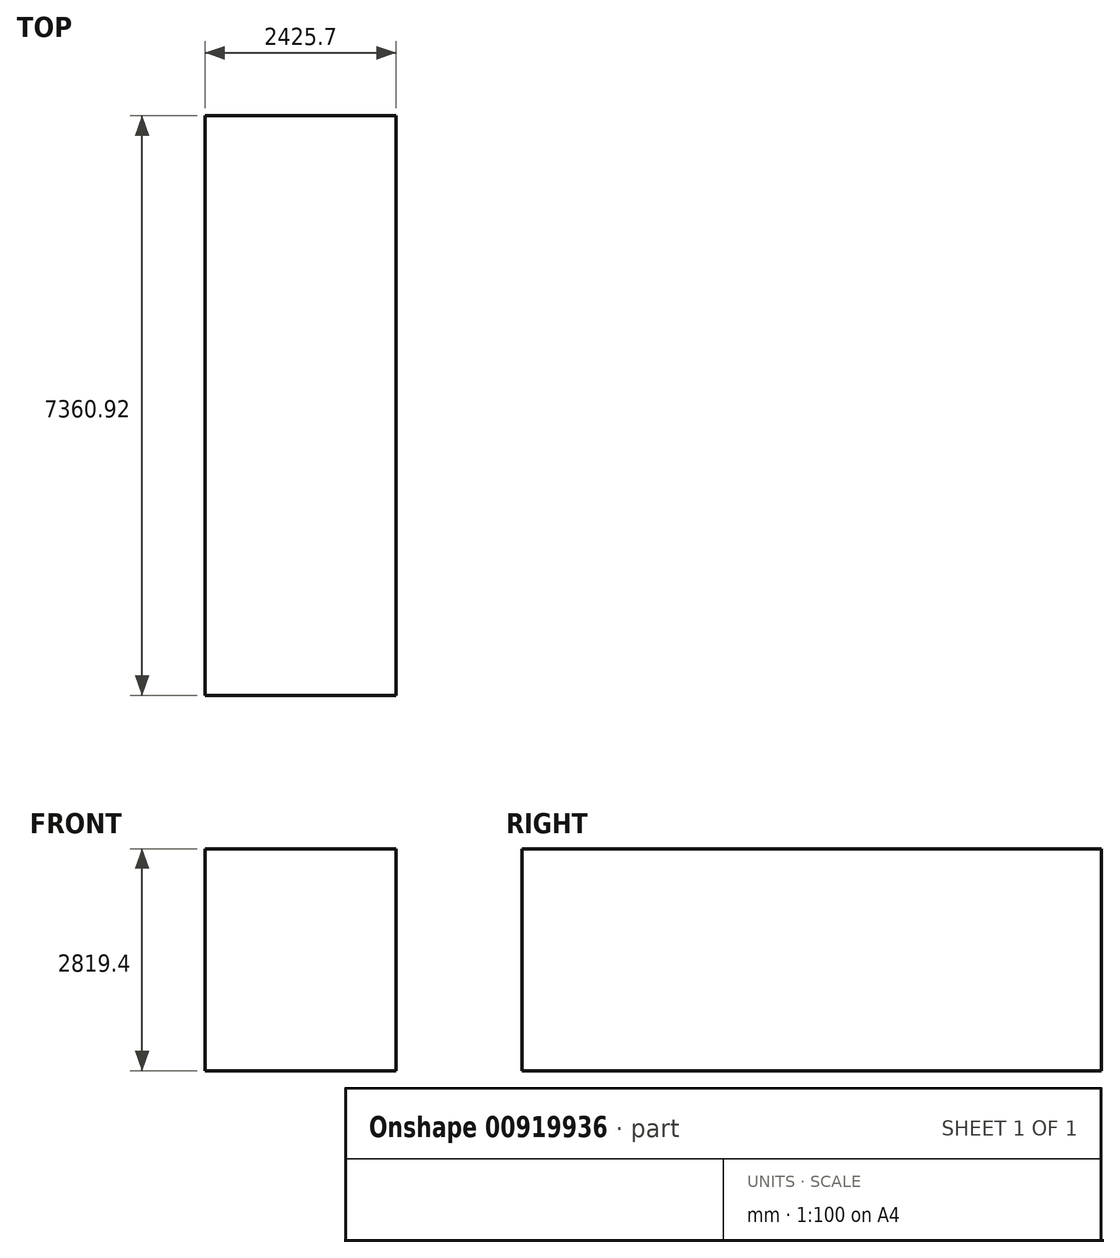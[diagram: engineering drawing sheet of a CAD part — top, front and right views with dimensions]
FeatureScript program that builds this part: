
annotation { "Feature Type Name" : "Feature", "Feature Type Description" : "" }
export const myFeature = defineFeature(function(context is Context, id is Id, definition is map)
    precondition{}
    {
        {
            var Q0;
            Q0=qCreatedBy(makeId("Top.planeOp"),FACE);
            var sketch = newSketch(context, id + "F0", { "sketchPlane" : qUnion([Q0])});
            skLineSegment(sketch, "E0.bottom", {"start": v(-1216, 5281.29) * mm, "end": v(1209.7, 5281.29) * mm});
            skLineSegment(sketch, "E0.top", {"start": v(-1216, -2079.63) * mm, "end": v(1209.7, -2079.63) * mm});
            skLineSegment(sketch, "E0.left", {"start": v(-1216, 5281.29) * mm, "end": v(-1216, -2079.63) * mm});
            skLineSegment(sketch, "E0.right", {"start": v(1209.7, 5281.29) * mm, "end": v(1209.7, -2079.63) * mm});
            skSolve(sketch);
        }
        {
            var Q0;
            Q0=makeQuery(id+"F0.imprint","IMPRINT",FACE,{"disambiguationData":[TD([[makeQuery(id+"F0.imprint","IMPRINT",EDGE,{"derivedFrom":sQuery(id+"F0.wireOp",EDGE,"E0.bottom")}),-1.0]])]});
            extrude(context, id + "F1", {"entities" : qUnion([Q0]), "depth" : 2819.4 * mm, "offsetDistance" : 25.4 * mm});
        }
    });
